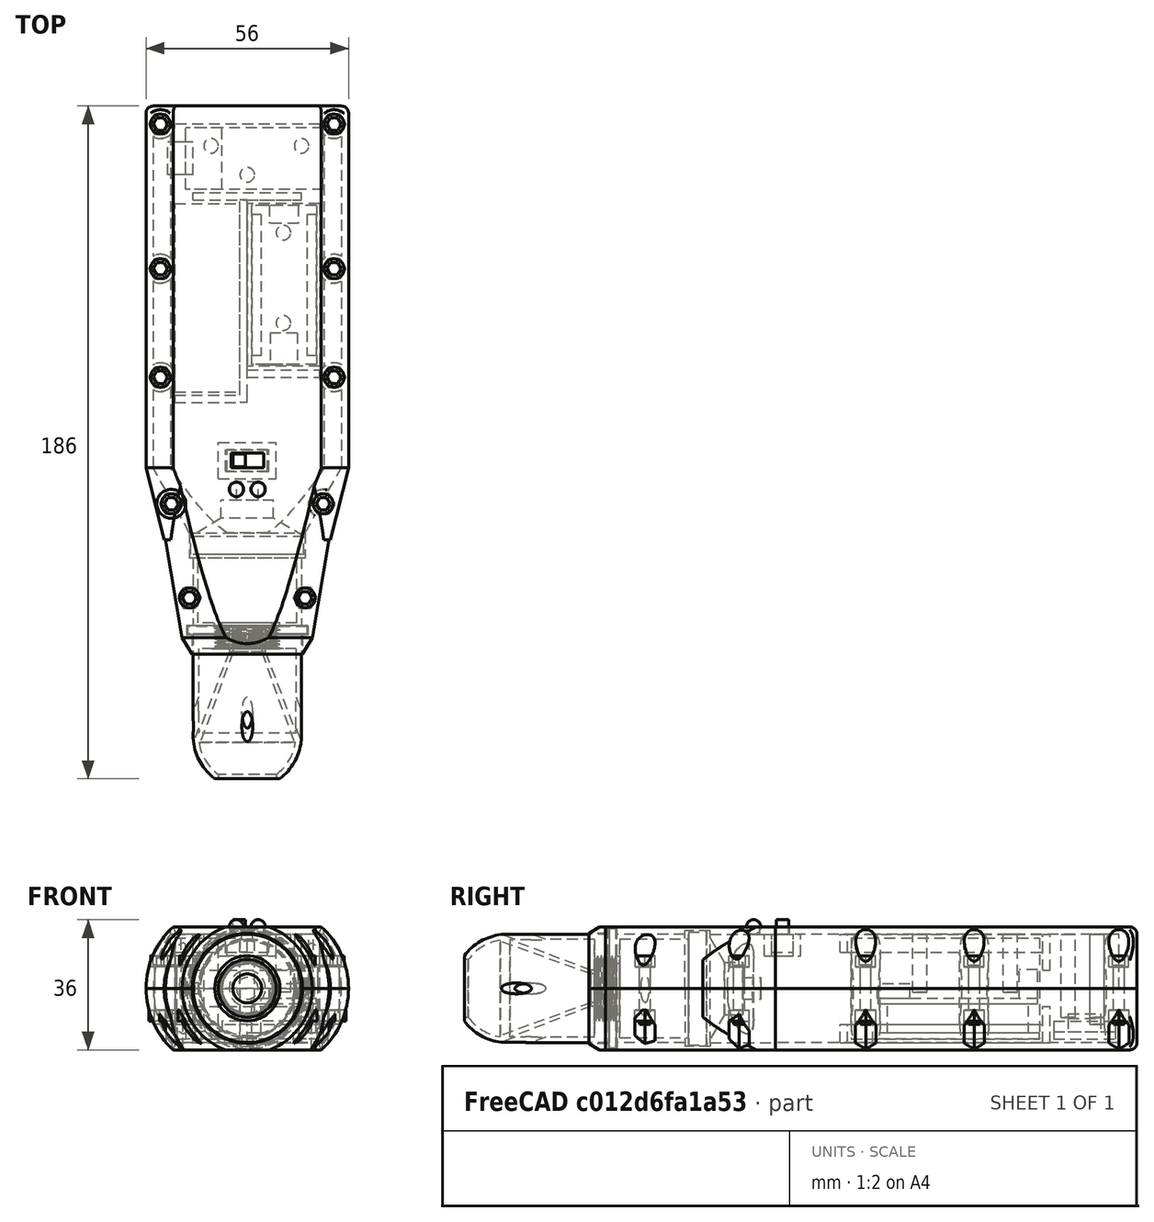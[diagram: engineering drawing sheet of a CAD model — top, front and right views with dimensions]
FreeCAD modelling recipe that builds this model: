
FCSTD DOCUMENT  (FreeCAD 0.15R4671 (Git))
Label: NitroxAnalyzer
License: All rights reserved
LicenseURL: http://en.wikipedia.org/wiki/All_rights_reserved
objects: Part::Cylinder×71, Part::MultiFuse×69, Part::Feature×42, Part::Box×36, Part::Cut×30, Part::Cone×12, Raytracing::RayFeature×11, Part::Sphere×4, Part::Fillet×2, Part::MultiCommon×2, Part::RegularPolygon×2, Part::Extrusion×2, Raytracing::RayProject×1
note: 272 computed .brp shape members not serialized (recipe doc carries the construction recipe); baked Part::Feature solids carry a one-line shape summary decoded from their .brp

FEATURE [Part::Cylinder] Cylinder
  Angle = 360
  Height = 2
  Placement = pos=(0,46,0) rot=(1,0,0;1.5708rad)
  Radius = 16.5
FEATURE [Part::Cylinder] Cylinder001
  Angle = 360
  Height = 28
  Placement = pos=(0,44,0) rot=(1,0,0;1.5708rad)
  Radius = 15
FEATURE [Part::Sphere] Sphere
  Angle1 = -90
  Angle2 = 90
  Angle3 = 180
  Placement = pos=(0,16,0) rot=(0,0,1;3.14159rad)
  Radius = 15
FEATURE [Part::Sphere] Sphere001
  Angle1 = -90
  Angle2 = 90
  Angle3 = 180
  Placement = pos=(0,16,0) rot=(0,0,1;3.14159rad)
  Radius = 13.5
FEATURE [Part::Cut] Cut
  Base = -> Sphere
  Tool = -> Sphere001
FEATURE [Part::Box] Box  label="Cube"
  Height = 30
  Length = 30
  Placement = pos=(-15,-6,-15) rot=(0,0,1;0rad)
  Width = 10
FEATURE [Part::Cut] Cut001
  Base = -> Cut
  Tool = -> Box
FEATURE [Part::Cylinder] Cylinder002
  Angle = 360
  Height = 24
  Placement = pos=(0,40,0) rot=(1,0,0;1.5708rad)
  Radius = 13.5
FEATURE [Part::Cut] Cut002
  Base = -> Cylinder001
  Tool = -> Cylinder002
FEATURE [Part::MultiFuse] Fusion
  Shapes = -> [Cut002,Cut001]
FEATURE [Part::Feature] Cut003
  Placement = pos=(-50,16,-24) rot=(0,0,1;0rad)
  shape: bbox 28.06 x 6.962 x 28.06 mm, 14 faces (baked)
FEATURE [Part::Cylinder] Cylinder003
  Angle = 360
  Height = 6
  Placement = pos=(0,46,0) rot=(1,0,0;1.5708rad)
  Radius = 10
FEATURE [Part::MultiFuse] Fusion001
  Shapes = -> [Cylinder,Fusion]
FEATURE [Part::Cut] Cut004
  Base = -> Fusion001
  Tool = -> Cylinder003
FEATURE [Part::MultiFuse] Fusion002
  Shapes = -> [Cut004,Cut003]
FEATURE [Part::Cone] Cone
  Angle = 360
  Height = 25
  Placement = pos=(0,46,0) rot=(1,0,0;1.5708rad)
  Radius1 = 5
  Radius2 = 14.5
FEATURE [Part::Cone] Cone001
  Angle = 360
  Height = 25
  Placement = pos=(0,46,0) rot=(1,0,0;1.5708rad)
  Radius1 = 4
  Radius2 = 13
FEATURE [Part::Cut] Cut005
  Base = -> Cone
  Placement = pos=(0,-7,0) rot=(0,0,1;0rad)
  Tool = -> Cone001
FEATURE [Part::Cylinder] Cylinder004
  Angle = 360
  Height = 7
  Placement = pos=(0,46,0) rot=(1,0,0;1.5708rad)
  Radius = 5
FEATURE [Part::Cylinder] Cylinder005
  Angle = 360
  Height = 7
  Placement = pos=(0,46,0) rot=(1,0,0;1.5708rad)
  Radius = 4
FEATURE [Part::Cut] Cut006
  Base = -> Cylinder004
  Tool = -> Cylinder005
FEATURE [Part::MultiFuse] Fusion003
  Shapes = -> [Cut005,Cut006]
FEATURE [Part::MultiFuse] Fusion004
  Shapes = -> [Fusion002,Fusion003]
FEATURE [Part::Cylinder] Cylinder006
  Angle = 360
  Height = 50
  Placement = pos=(0,37,8) rot=(1,0,0;1.213rad)
  Radius = 1.5
FEATURE [Part::Feature] Cylinder007
  Placement = pos=(0,0,0) rot=(0,1,0;1.5708rad)
  shape: bbox 20.32 x 47.88 x 3 mm, 3 faces (baked)
FEATURE [Part::Feature] Cylinder008
  Placement = pos=(0,0,0) rot=(0,1,0;3.14159rad)
  shape: bbox 3 x 47.88 x 20.32 mm, 3 faces (baked)
FEATURE [Part::Feature] Cylinder009
  Placement = pos=(0,0,0) rot=(0,-1,0;1.5708rad)
  shape: bbox 20.32 x 47.88 x 3 mm, 3 faces (baked)
FEATURE [Part::MultiFuse] Fusion005
  Shapes = -> [Cylinder009,Cylinder008,Cylinder007,Cylinder006]
FEATURE [Part::Cut] Cut007
  Base = -> Fusion004
  Tool = -> Fusion005
FEATURE [Part::Cylinder] Cylinder010
  Angle = 360
  Height = 18
  Placement = pos=(0,10,0) rot=(1,0,0;1.5708rad)
  Radius = 8
FEATURE [Part::Cut] Cut008  label="o2-cell-support"
  Base = -> Cut007
  Tool = -> Cylinder010
FEATURE [Part::Feature] Fusion006  label="o2_cell"
  Placement = pos=(-62,-6,-24) rot=(0,0,1;0rad)
  shape: bbox 31.3 x 45 x 31.3 mm, 15 faces (baked)
FEATURE [Part::Box] Box004  label="battery"
  Height = 18
  Length = 28
  Placement = pos=(-20,111,14) rot=(0,1,0;1.5708rad)
  Width = 52
FEATURE [Part::Cylinder] Cylinder032
  Angle = 360
  Height = 100
  Placement = pos=(5,190,0) rot=(1,0,0;1.5708rad)
  Radius = 23
FEATURE [Part::Cylinder] Cylinder033
  Angle = 360
  Height = 100
  Placement = pos=(-5,190,0) rot=(1,0,0;1.5708rad)
  Radius = 23
FEATURE [Part::MultiFuse] Fusion017
  Shapes = -> [Cylinder033,Cylinder032]
FEATURE [Part::Box] Box012  label="Cube010"
  Height = 18
  Length = 47
  Placement = pos=(-24,0,17) rot=(0,0,1;0rad)
  Width = 200
FEATURE [Part::Box] Box013  label="Cube011"
  Height = 18
  Length = 47
  Placement = pos=(-24,0,-35) rot=(0,0,1;0rad)
  Width = 200
FEATURE [Part::MultiFuse] Fusion018
  Shapes = -> [Box013,Box012]
FEATURE [Part::Cone] Cone006
  Angle = 360
  Height = 20
  Placement = pos=(5,70,0) rot=(-1,0,0;1.5708rad)
  Radius1 = 18
  Radius2 = 23
FEATURE [Part::Cone] Cone007
  Angle = 360
  Height = 20
  Placement = pos=(-5,70,0) rot=(-1,0,0;1.5708rad)
  Radius1 = 18
  Radius2 = 23
FEATURE [Part::Cone] Cone008
  Angle = 360
  Height = 47
  Placement = pos=(0,43,0) rot=(-1,0,0;1.5708rad)
  Radius1 = 18
  Radius2 = 26
FEATURE [Part::MultiFuse] Fusion019
  Shapes = -> [Cone008,Cone007,Cone006]
FEATURE [Part::MultiFuse] Fusion020
  Shapes = -> [Fusion017,Fusion019]
FEATURE [Part::Cut] Cut026
  Base = -> Fusion020
  Tool = -> Fusion018
FEATURE [Part::Cylinder] Cylinder038
  Angle = 360
  Height = 6
  Placement = pos=(0,44,0) rot=(1,0,0;1.5708rad)
  Radius = 15.25
FEATURE [Part::Cone] Cone016
  Angle = 360
  Height = 5
  Placement = pos=(0,38,0) rot=(-1,0,0;1.5708rad)
  Radius1 = 15
  Radius2 = 18
FEATURE [Part::Box] Box016  label="Cube014"
  Height = 18
  Length = 47
  Placement = pos=(-24,0,15) rot=(0,0,1;0rad)
  Width = 200
FEATURE [Part::Box] Box017  label="Cube015"
  Height = 18
  Length = 47
  Placement = pos=(-24,0,-33) rot=(0,0,1;0rad)
  Width = 200
FEATURE [Part::MultiFuse] Fusion029
  Shapes = -> [Box017,Box016]
FEATURE [Part::Cylinder] Cylinder039
  Angle = 360
  Height = 20
  Placement = pos=(0,65,0) rot=(1,0,0;1.5708rad)
  Radius = 15
FEATURE [Part::Cylinder] Cylinder040
  Angle = 360
  Height = 2.5
  Placement = pos=(0,46.25,0) rot=(1,0,0;1.5708rad)
  Radius = 16.75
FEATURE [Part::Cylinder] Cylinder041
  Angle = 360
  Height = 7
  Placement = pos=(0,72,0) rot=(1,0,0;1.5708rad)
  Radius = 16
FEATURE [Part::Cone] Cone017
  Angle = 360
  Height = 18
  Placement = pos=(0,72,0) rot=(-1,0,0;1.5708rad)
  Radius1 = 16
  Radius2 = 26
FEATURE [Part::Box] Box018  label="Cube016"
  Height = 15
  Length = 47
  Placement = pos=(-24,0,15) rot=(0,0,1;0rad)
  Width = 200
FEATURE [Part::Box] Box019  label="Cube017"
  Height = 15
  Length = 47
  Placement = pos=(-24,0,-30) rot=(0,0,1;0rad)
  Width = 200
FEATURE [Part::MultiFuse] Fusion030
  Shapes = -> [Box019,Box018]
FEATURE [Part::Cylinder] Cylinder042
  Angle = 360
  Height = 95
  Placement = pos=(0,185,0) rot=(1,0,0;1.5708rad)
  Radius = 26
FEATURE [Part::MultiFuse] Fusion031
  Shapes = -> [Cone017,Cylinder042]
FEATURE [Part::Cut] Cut031
  Base = -> Fusion031
  Tool = -> Fusion030
FEATURE [Part::MultiFuse] Fusion032
  Shapes = -> [Cylinder039,Cylinder040,Cylinder041,Cut031]
FEATURE [Part::Box] Box020  label="Cube018"
  Height = 1.6
  Length = 20
  Width = 45
FEATURE [Part::Box] Box021  label="Cube019"
  Height = 8
  Length = 2.54
  Width = 39
FEATURE [Part::Box] Box022  label="Cube020"
  Height = 8
  Length = 2.54
  Placement = pos=(15.24,0,0) rot=(0,0,1;0rad)
  Width = 39
FEATURE [Part::MultiFuse] Fusion036
  Placement = pos=(1,3,1.6) rot=(0,0,1;0rad)
  Shapes = -> [Box022,Box021]
FEATURE [Part::Box] Box023  label="Cube021"
  Height = 1.6
  Length = 18
  Placement = pos=(0.9,0.5,9.6) rot=(0,0,1;0rad)
  Width = 44
FEATURE [Part::Box] Box024  label="Cube022"
  Height = 8
  Length = 8
  Placement = pos=(5.9,0.5,11.2) rot=(0,0,1;0rad)
  Width = 5
FEATURE [Part::Box] Box025  label="Cube023"
  Height = 4
  Length = 7.5
  Placement = pos=(6.175,35.75,11.2) rot=(0,0,1;0rad)
  Width = 9
FEATURE [Part::MultiFuse] Fusion037  label="arduino nano"
  Shapes = -> [Box024,Box023,Box025]
FEATURE [Part::MultiFuse] Fusion038  label="nano support"
  Shapes = -> [Fusion036,Box020]
FEATURE [Part::MultiFuse] Fusion039  label="nano board"
  Placement = pos=(20,163,-14) rot=(0,0,1;3.14159rad)
  Shapes = -> [Fusion038,Fusion037]
FEATURE [Part::Feature] Fusion042  label="BT006"
  Placement = pos=(111,164,-43) rot=(0,0,1;1.5708rad)
  shape: bbox 43 x 17 x 7 mm, 14 faces (baked)
FEATURE [Part::MultiFuse] Fusion043
  Shapes = -> [Cut026,Cone016]
FEATURE [Part::Cut] Cut032
  Base = -> Fusion043
  Tool = -> Cylinder038
FEATURE [Part::Cut] Cut033
  Base = -> Cut032
  Tool = -> Fusion029
FEATURE [Part::Cut] Cut034
  Base = -> Cut033
  Tool = -> Fusion032
FEATURE [Part::Fillet] Fillet  label="BOX"
  Base = -> Cut034
  Edges = 5 edges r=2: [Edge15,Edge25,Edge38,Edge39,Edge40]
FEATURE [Part::Box] Box026  label="Cube024"
  Height = 10
  Length = 30
  Placement = pos=(-15,164,-15) rot=(0,0,1;0rad)
  Width = 2
FEATURE [Part::Cylinder] Cylinder043
  Angle = 360
  Height = 23
  Placement = pos=(15,179,-8) rot=(0,0,1;0rad)
  Radius = 2
FEATURE [Part::Cylinder] Cylinder044
  Angle = 360
  Height = 23
  Placement = pos=(0,171,-8) rot=(0,0,1;0rad)
  Radius = 2
FEATURE [Part::Cylinder] Cylinder045
  Angle = 360
  Height = 25
  Placement = pos=(-10,179,-10) rot=(0,0,1;0rad)
  Radius = 2
FEATURE [Part::Box] Box028  label="Cube026"
  Height = 5
  Length = 56
  Placement = pos=(0,108,-15) rot=(0,0,1;1.5708rad)
  Width = 2
FEATURE [Part::Box] Box029  label="Cube027"
  Height = 5
  Length = 20
  Placement = pos=(-20,108,-15) rot=(0,0,1;0rad)
  Width = 2
FEATURE [Part::Cylinder] Cylinder046
  Angle = 360
  Height = 16
  Placement = pos=(10,144,-1) rot=(0,0,1;0rad)
  Radius = 2
FEATURE [Part::Box] Box030  label="Cube028"
  Height = 5
  Length = 20
  Placement = pos=(0,115,-15) rot=(0,0,1;0rad)
  Width = 2
FEATURE [Part::Box] Box031  label="Cube029"
  Height = 4
  Length = 3.5
  Placement = pos=(2,1.25,5) rot=(0,0,1;0rad)
  Width = 3.5
FEATURE [Part::Box] Box032  label="Cube030"
  Height = 5
  Length = 12
  Width = 6
FEATURE [Part::MultiFuse] Fusion044  label="power-switch"
  Placement = pos=(-6,89,10) rot=(0,0,1;0rad)
  Shapes = -> [Box032,Box031]
FEATURE [Part::Box] Box033  label="Cube031"
  Height = 4
  Length = 9
  Placement = pos=(-4.5,90,14) rot=(0,0,1;0rad)
  Width = 4
FEATURE [Part::Cut] Cut035  label="BOTTOM_BOX"
  Base = -> Fillet
  Tool = -> Box033
FEATURE [Part::Cylinder] Cylinder047
  Angle = 360
  Height = 40
  Placement = pos=(-16,54,-20) rot=(0,0,1;0rad)
  Radius = 1.5
FEATURE [Part::Cylinder] Cylinder048
  Angle = 360
  Height = 40
  Placement = pos=(16,54,-20) rot=(0,0,1;0rad)
  Radius = 1.5
FEATURE [Part::Cylinder] Cylinder049
  Angle = 360
  Height = 40
  Placement = pos=(-21,80,-20) rot=(0,0,1;0rad)
  Radius = 1.5
FEATURE [Part::Cylinder] Cylinder050
  Angle = 360
  Height = 40
  Placement = pos=(24,115,-20) rot=(0,0,1;0rad)
  Radius = 1.5
FEATURE [Part::Cylinder] Cylinder051
  Angle = 360
  Height = 40
  Placement = pos=(21,80,-20) rot=(0,0,1;0rad)
  Radius = 1.5
FEATURE [Part::Cylinder] Cylinder052
  Angle = 360
  Height = 40
  Placement = pos=(-24,115,-20) rot=(0,0,1;0rad)
  Radius = 1.5
FEATURE [Part::Cylinder] Cylinder053
  Angle = 360
  Height = 40
  Placement = pos=(24,115,-20) rot=(0,0,1;0rad)
  Radius = 1.5
FEATURE [Part::Cylinder] Cylinder054
  Angle = 360
  Height = 40
  Placement = pos=(-24,115,-20) rot=(0,0,1;0rad)
  Radius = 1.5
FEATURE [Part::MultiFuse] Fusion045
  Placement = pos=(0,30,0) rot=(0,0,1;0rad)
  Shapes = -> [Cylinder054,Cylinder053]
FEATURE [Part::Cylinder] Cylinder055
  Angle = 360
  Height = 40
  Placement = pos=(24,115,-20) rot=(0,0,1;0rad)
  Radius = 1.5
FEATURE [Part::Cylinder] Cylinder056
  Angle = 360
  Height = 40
  Placement = pos=(-24,115,-20) rot=(0,0,1;0rad)
  Radius = 1.5
FEATURE [Part::MultiFuse] Fusion046
  Placement = pos=(0,70,0) rot=(0,0,1;0rad)
  Shapes = -> [Cylinder056,Cylinder055]
FEATURE [Part::MultiFuse] Fusion047  label="holes"
  Shapes = -> [Fusion046,Fusion045,Cylinder052,Cylinder051,Cylinder050,Cylinder049,Cylinder048,Cylinder047]
FEATURE [Part::Cylinder] Cylinder057
  Angle = 360
  Height = 100
  Placement = pos=(5,190,0) rot=(1,0,0;1.5708rad)
  Radius = 23
FEATURE [Part::Cylinder] Cylinder058
  Angle = 360
  Height = 100
  Placement = pos=(-5,190,0) rot=(1,0,0;1.5708rad)
  Radius = 23
FEATURE [Part::MultiFuse] Fusion048
  Shapes = -> [Cylinder058,Cylinder057]
FEATURE [Part::Box] Box034  label="Cube032"
  Height = 18
  Length = 47
  Placement = pos=(-24,0,17) rot=(0,0,1;0rad)
  Width = 200
FEATURE [Part::Box] Box035  label="Cube033"
  Height = 18
  Length = 47
  Placement = pos=(-24,0,-35) rot=(0,0,1;0rad)
  Width = 200
FEATURE [Part::MultiFuse] Fusion049
  Shapes = -> [Box035,Box034]
FEATURE [Part::Cone] Cone018
  Angle = 360
  Height = 20
  Placement = pos=(5,70,0) rot=(-1,0,0;1.5708rad)
  Radius1 = 18
  Radius2 = 23
FEATURE [Part::Cone] Cone019
  Angle = 360
  Height = 20
  Placement = pos=(-5,70,0) rot=(-1,0,0;1.5708rad)
  Radius1 = 18
  Radius2 = 23
FEATURE [Part::Cone] Cone020
  Angle = 360
  Height = 47
  Placement = pos=(0,43,0) rot=(-1,0,0;1.5708rad)
  Radius1 = 18
  Radius2 = 26
FEATURE [Part::MultiFuse] Fusion050
  Shapes = -> [Cone020,Cone019,Cone018]
FEATURE [Part::MultiFuse] Fusion051
  Shapes = -> [Fusion048,Fusion050]
FEATURE [Part::Cut] Cut036
  Base = -> Fusion051
  Tool = -> Fusion049
FEATURE [Part::Cylinder] Cylinder059
  Angle = 360
  Height = 6
  Placement = pos=(0,44,0) rot=(1,0,0;1.5708rad)
  Radius = 15.25
FEATURE [Part::Cone] Cone021
  Angle = 360
  Height = 5
  Placement = pos=(0,38,0) rot=(-1,0,0;1.5708rad)
  Radius1 = 15
  Radius2 = 18
FEATURE [Part::Box] Box036  label="Cube034"
  Height = 18
  Length = 47
  Placement = pos=(-24,0,15) rot=(0,0,1;0rad)
  Width = 200
FEATURE [Part::Box] Box037  label="Cube035"
  Height = 18
  Length = 47
  Placement = pos=(-24,0,-33) rot=(0,0,1;0rad)
  Width = 200
FEATURE [Part::MultiFuse] Fusion052
  Shapes = -> [Box037,Box036]
FEATURE [Part::Cylinder] Cylinder060
  Angle = 360
  Height = 20
  Placement = pos=(0,65,0) rot=(1,0,0;1.5708rad)
  Radius = 15
FEATURE [Part::Cylinder] Cylinder061
  Angle = 360
  Height = 2.5
  Placement = pos=(0,46.25,0) rot=(1,0,0;1.5708rad)
  Radius = 16.75
FEATURE [Part::Cylinder] Cylinder062
  Angle = 360
  Height = 7
  Placement = pos=(0,72,0) rot=(1,0,0;1.5708rad)
  Radius = 16
FEATURE [Part::Cone] Cone022
  Angle = 360
  Height = 18
  Placement = pos=(0,72,0) rot=(-1,0,0;1.5708rad)
  Radius1 = 16
  Radius2 = 26
FEATURE [Part::Box] Box038  label="Cube036"
  Height = 15
  Length = 47
  Placement = pos=(-24,0,15) rot=(0,0,1;0rad)
  Width = 200
FEATURE [Part::Box] Box039  label="Cube037"
  Height = 15
  Length = 47
  Placement = pos=(-24,0,-30) rot=(0,0,1;0rad)
  Width = 200
FEATURE [Part::MultiFuse] Fusion053
  Shapes = -> [Box039,Box038]
FEATURE [Part::Cylinder] Cylinder063
  Angle = 360
  Height = 95
  Placement = pos=(0,185,0) rot=(1,0,0;1.5708rad)
  Radius = 26
FEATURE [Part::MultiFuse] Fusion054
  Shapes = -> [Cone022,Cylinder063]
FEATURE [Part::Cut] Cut037
  Base = -> Fusion054
  Tool = -> Fusion053
FEATURE [Part::MultiFuse] Fusion055
  Shapes = -> [Cylinder060,Cylinder061,Cylinder062,Cut037]
FEATURE [Part::MultiFuse] Fusion056
  Shapes = -> [Cut036,Cone021]
FEATURE [Part::Cut] Cut038
  Base = -> Fusion056
  Tool = -> Cylinder059
FEATURE [Part::Cut] Cut039
  Base = -> Cut038
  Tool = -> Fusion052
FEATURE [Part::Cut] Cut040
  Base = -> Cut039
  Tool = -> Fusion055
FEATURE [Part::Fillet] Fillet001  label="BOX001"
  Base = -> Cut040
  Edges = 5 edges r=2: [Edge15,Edge25,Edge38,Edge39,Edge40]
FEATURE [Part::Box] Box040  label="Cube038"
  Height = 4
  Length = 9
  Placement = pos=(-4.5,90,14) rot=(0,0,1;0rad)
  Width = 4
FEATURE [Part::Cut] Cut041  label="TOP_BOX"
  Base = -> Fillet001
  Tool = -> Box040
FEATURE [Part::Box] Box041  label="Cube039"
  Height = 30
  Length = 100
  Placement = pos=(-39,-4,0) rot=(0,0,1;0rad)
  Width = 300
FEATURE [Part::Cut] Cut042
  Base = -> Cut035
  Tool = -> Box041
FEATURE [Part::Cylinder] Cylinder064
  Angle = 360
  Height = 40
  Placement = pos=(-16,54,-20) rot=(0,0,1;0rad)
  Radius = 1.5
FEATURE [Part::Cylinder] Cylinder065
  Angle = 360
  Height = 40
  Placement = pos=(16,54,-20) rot=(0,0,1;0rad)
  Radius = 1.5
FEATURE [Part::Cylinder] Cylinder066
  Angle = 360
  Height = 40
  Placement = pos=(-21,80,-20) rot=(0,0,1;0rad)
  Radius = 4
FEATURE [Part::Cylinder] Cylinder067
  Angle = 360
  Height = 40
  Placement = pos=(24,115,-20) rot=(0,0,1;0rad)
  Radius = 4
FEATURE [Part::Cylinder] Cylinder068
  Angle = 360
  Height = 40
  Placement = pos=(21,80,-20) rot=(0,0,1;0rad)
  Radius = 4
FEATURE [Part::Cylinder] Cylinder069
  Angle = 360
  Height = 40
  Placement = pos=(-24,115,-20) rot=(0,0,1;0rad)
  Radius = 4
FEATURE [Part::Cylinder] Cylinder070
  Angle = 360
  Height = 40
  Placement = pos=(24,115,-20) rot=(0,0,1;0rad)
  Radius = 4
FEATURE [Part::Cylinder] Cylinder071
  Angle = 360
  Height = 40
  Placement = pos=(-24,115,-20) rot=(0,0,1;0rad)
  Radius = 4
FEATURE [Part::MultiFuse] Fusion057
  Placement = pos=(0,30,0) rot=(0,0,1;0rad)
  Shapes = -> [Cylinder071,Cylinder070]
FEATURE [Part::Cylinder] Cylinder072
  Angle = 360
  Height = 40
  Placement = pos=(24,115,-20) rot=(0,0,1;0rad)
  Radius = 4
FEATURE [Part::Cylinder] Cylinder073
  Angle = 360
  Height = 40
  Placement = pos=(-24,115,-20) rot=(0,0,1;0rad)
  Radius = 4
FEATURE [Part::MultiFuse] Fusion058
  Placement = pos=(0,70,0) rot=(0,0,1;0rad)
  Shapes = -> [Cylinder073,Cylinder072]
FEATURE [Part::MultiFuse] Fusion059
  Placement = pos=(0,0,-20) rot=(0,0,1;0rad)
  Shapes = -> [Fusion058,Fusion057,Cylinder069,Cylinder068,Cylinder067,Cylinder066,Cylinder065,Cylinder064]
FEATURE [Part::MultiFuse] Fusion060
  Shapes = -> [Box030,Box029,Box028,Box026]
FEATURE [Part::Box] Box042  label="Cube040"
  Height = 80
  Length = 60
  Placement = pos=(-30,0,-80) rot=(0,0,1;0rad)
  Width = 200
FEATURE [Part::Feature] Cut043
  shape: bbox 56 x 147 x 47.44 mm, 14 faces (baked)
FEATURE [Part::MultiCommon] Common
  Shapes = -> [Fusion059,Cut043]
FEATURE [Part::MultiFuse] Fusion061
  Shapes = -> [Cut042,Common]
FEATURE [Part::Cut] Cut044
  Base = -> Fusion061
  Tool = -> Fusion047
FEATURE [Part::Cylinder] Cylinder074
  Angle = 360
  Height = 16
  Placement = pos=(0,0,-9) rot=(0,0,1;0rad)
  Radius = 1.5
FEATURE [Part::Feature] Extrude001
  Placement = pos=(21,80,-36) rot=(0,0,1;0rad)
  shape: bbox 6.5 x 5.629 x 30 mm, 8 faces (baked)
FEATURE [Part::Cylinder] Cylinder075
  Angle = 360
  Height = 3
  Placement = pos=(0,0,7) rot=(0,0,1;0rad)
  Radius = 2.75
FEATURE [Part::MultiFuse] Fusion062
  Placement = pos=(16,54,-1) rot=(0,0,1;0rad)
  Shapes = -> [Cylinder075,Cylinder074]
FEATURE [Part::Feature] Extrude002
  Placement = pos=(-21,80,-36) rot=(0,0,1;0rad)
  shape: bbox 6.5 x 5.629 x 30 mm, 8 faces (baked)
FEATURE [Part::MultiFuse] Fusion063
  Shapes = -> [Extrude002,Extrude001]
FEATURE [Part::Feature] Extrude003
  Placement = pos=(24,80,-36) rot=(0,0,1;0rad)
  shape: bbox 6.5 x 5.629 x 30 mm, 8 faces (baked)
FEATURE [Part::Feature] Extrude004
  Placement = pos=(-24,80,-36) rot=(0,0,1;0rad)
  shape: bbox 6.5 x 5.629 x 30 mm, 8 faces (baked)
FEATURE [Part::MultiFuse] Fusion064
  Placement = pos=(0,35,0) rot=(0,0,1;0rad)
  Shapes = -> [Extrude004,Extrude003]
FEATURE [Part::Feature] Fusion065
  Placement = pos=(0,30,0) rot=(0,0,1;0rad)
  shape: bbox 54.5 x 5.629 x 30 mm, 16 faces, 2 solids (baked)
FEATURE [Part::Feature] Fusion066
  Placement = pos=(0,70,0) rot=(0,0,1;0rad)
  shape: bbox 54.5 x 5.629 x 30 mm, 16 faces, 2 solids (baked)
FEATURE [Part::MultiFuse] Fusion067
  Shapes = -> [Fusion066,Fusion065,Fusion064,Fusion063]
FEATURE [Part::Feature] Extrude005
  Placement = pos=(16,54,-36) rot=(0,0,1;0rad)
  shape: bbox 6.5 x 5.629 x 30 mm, 8 faces (baked)
FEATURE [Part::Cut] Cut045
  Base = -> Cut044
  Tool = -> Fusion067
FEATURE [Part::Feature] Extrude006
  Placement = pos=(-16,54,-36) rot=(0,0,1;0rad)
  shape: bbox 6.5 x 5.629 x 30 mm, 8 faces (baked)
FEATURE [Part::MultiFuse] Fusion068
  Shapes = -> [Extrude006,Extrude005]
FEATURE [Part::Cut] Cut046  label="box bottomdaf"
  Base = -> Cut045
  Tool = -> Fusion068
FEATURE [Part::MultiFuse] Fusion069  label="box-bottom"
  Shapes = -> [Fusion060,Cut046]
FEATURE [Part::Cut] Cut047
  Base = -> Cut041
  Tool = -> Box042
FEATURE [Part::Cylinder] Cylinder076
  Angle = 360
  Height = 40
  Placement = pos=(-16,54,-20) rot=(0,0,1;0rad)
  Radius = 1.5
FEATURE [Part::Cylinder] Cylinder077
  Angle = 360
  Height = 40
  Placement = pos=(16,54,-20) rot=(0,0,1;0rad)
  Radius = 1.5
FEATURE [Part::Cylinder] Cylinder078
  Angle = 360
  Height = 40
  Placement = pos=(-21,80,-20) rot=(0,0,1;0rad)
  Radius = 1.5
FEATURE [Part::Cylinder] Cylinder079
  Angle = 360
  Height = 40
  Placement = pos=(24,115,-20) rot=(0,0,1;0rad)
  Radius = 1.5
FEATURE [Part::Cylinder] Cylinder080
  Angle = 360
  Height = 40
  Placement = pos=(21,80,-20) rot=(0,0,1;0rad)
  Radius = 1.5
FEATURE [Part::Cylinder] Cylinder081
  Angle = 360
  Height = 40
  Placement = pos=(-24,115,-20) rot=(0,0,1;0rad)
  Radius = 1.5
FEATURE [Part::Cylinder] Cylinder082
  Angle = 360
  Height = 40
  Placement = pos=(24,115,-20) rot=(0,0,1;0rad)
  Radius = 1.5
FEATURE [Part::Cylinder] Cylinder083
  Angle = 360
  Height = 40
  Placement = pos=(-24,115,-20) rot=(0,0,1;0rad)
  Radius = 1.5
FEATURE [Part::MultiFuse] Fusion070
  Placement = pos=(0,30,0) rot=(0,0,1;0rad)
  Shapes = -> [Cylinder083,Cylinder082]
FEATURE [Part::Cylinder] Cylinder084
  Angle = 360
  Height = 40
  Placement = pos=(24,115,-20) rot=(0,0,1;0rad)
  Radius = 1.5
FEATURE [Part::Cylinder] Cylinder085
  Angle = 360
  Height = 40
  Placement = pos=(-24,115,-20) rot=(0,0,1;0rad)
  Radius = 1.5
FEATURE [Part::MultiFuse] Fusion071
  Placement = pos=(0,70,0) rot=(0,0,1;0rad)
  Shapes = -> [Cylinder085,Cylinder084]
FEATURE [Part::MultiFuse] Fusion072  label="holes001"
  Shapes = -> [Fusion071,Fusion070,Cylinder081,Cylinder080,Cylinder079,Cylinder078,Cylinder077,Cylinder076]
FEATURE [Part::Cylinder] Cylinder086
  Angle = 360
  Height = 40
  Placement = pos=(-16,54,-20) rot=(0,0,1;0rad)
  Radius = 1.5
FEATURE [Part::Cylinder] Cylinder087
  Angle = 360
  Height = 40
  Placement = pos=(16,54,-20) rot=(0,0,1;0rad)
  Radius = 1.5
FEATURE [Part::Cylinder] Cylinder088
  Angle = 360
  Height = 40
  Placement = pos=(-21,80,-20) rot=(0,0,1;0rad)
  Radius = 4
FEATURE [Part::Cylinder] Cylinder089
  Angle = 360
  Height = 40
  Placement = pos=(24,115,-20) rot=(0,0,1;0rad)
  Radius = 4
FEATURE [Part::Cylinder] Cylinder090
  Angle = 360
  Height = 40
  Placement = pos=(21,80,-20) rot=(0,0,1;0rad)
  Radius = 4
FEATURE [Part::Cylinder] Cylinder091
  Angle = 360
  Height = 40
  Placement = pos=(-24,115,-20) rot=(0,0,1;0rad)
  Radius = 4
FEATURE [Part::Cylinder] Cylinder092
  Angle = 360
  Height = 40
  Placement = pos=(24,115,-20) rot=(0,0,1;0rad)
  Radius = 4
FEATURE [Part::Cylinder] Cylinder093
  Angle = 360
  Height = 40
  Placement = pos=(-24,115,-20) rot=(0,0,1;0rad)
  Radius = 4
FEATURE [Part::MultiFuse] Fusion073
  Placement = pos=(0,30,0) rot=(0,0,1;0rad)
  Shapes = -> [Cylinder093,Cylinder092]
FEATURE [Part::Cylinder] Cylinder094
  Angle = 360
  Height = 40
  Placement = pos=(24,115,-20) rot=(0,0,1;0rad)
  Radius = 4
FEATURE [Part::Cylinder] Cylinder095
  Angle = 360
  Height = 40
  Placement = pos=(-24,115,-20) rot=(0,0,1;0rad)
  Radius = 4
FEATURE [Part::MultiFuse] Fusion074
  Placement = pos=(0,70,0) rot=(0,0,1;0rad)
  Shapes = -> [Cylinder095,Cylinder094]
FEATURE [Part::MultiFuse] Fusion075
  Placement = pos=(0,0,20) rot=(0,0,1;0rad)
  Shapes = -> [Fusion074,Fusion073,Cylinder091,Cylinder090,Cylinder089,Cylinder088,Cylinder087,Cylinder086]
FEATURE [Part::Feature] Cut048
  shape: bbox 56 x 147 x 47.44 mm, 14 faces (baked)
FEATURE [Part::MultiCommon] Common001
  Shapes = -> [Fusion075,Cut048]
FEATURE [Part::MultiFuse] Fusion076
  Shapes = -> [Cut047,Common001]
FEATURE [Part::Cut] Cut049
  Base = -> Fusion076
  Tool = -> Fusion072
FEATURE [Part::Feature] Fusion078
  Placement = pos=(16,54,0) rot=(0,0,1;0rad)
  shape: bbox 5.5 x 5.5 x 31 mm, 5 faces (baked)
FEATURE [Part::Feature] Fusion079
  Placement = pos=(-16,54,0) rot=(0,0,1;0rad)
  shape: bbox 5.5 x 5.5 x 31 mm, 5 faces (baked)
FEATURE [Part::Feature] Fusion080
  Placement = pos=(-21,80,0) rot=(0,0,1;0rad)
  shape: bbox 5.5 x 5.5 x 31 mm, 5 faces (baked)
FEATURE [Part::Feature] Fusion081
  Placement = pos=(21,80,0) rot=(0,0,1;0rad)
  shape: bbox 5.5 x 5.5 x 31 mm, 5 faces (baked)
FEATURE [Part::Feature] Fusion082
  Placement = pos=(24,115,0) rot=(0,0,1;0rad)
  shape: bbox 5.5 x 5.5 x 31 mm, 5 faces (baked)
FEATURE [Part::Feature] Fusion083
  Placement = pos=(-24,115,0) rot=(0,0,1;0rad)
  shape: bbox 5.5 x 5.5 x 31 mm, 5 faces (baked)
FEATURE [Part::MultiFuse] Fusion084
  Shapes = -> [Fusion082,Fusion083]
FEATURE [Part::Feature] Fusion085
  Placement = pos=(24,115,0) rot=(0,0,1;0rad)
  shape: bbox 5.5 x 5.5 x 31 mm, 5 faces (baked)
FEATURE [Part::Feature] Fusion086
  Placement = pos=(-24,115,0) rot=(0,0,1;0rad)
  shape: bbox 5.5 x 5.5 x 31 mm, 5 faces (baked)
FEATURE [Part::MultiFuse] Fusion087
  Placement = pos=(0,30,0) rot=(0,0,1;0rad)
  Shapes = -> [Fusion085,Fusion086]
FEATURE [Part::Feature] Fusion088
  Placement = pos=(24,115,0) rot=(0,0,1;0rad)
  shape: bbox 5.5 x 5.5 x 31 mm, 5 faces (baked)
FEATURE [Part::Feature] Fusion089
  Placement = pos=(-24,115,0) rot=(0,0,1;0rad)
  shape: bbox 5.5 x 5.5 x 31 mm, 5 faces (baked)
FEATURE [Part::MultiFuse] Fusion090
  Placement = pos=(0,70,0) rot=(0,0,1;0rad)
  Shapes = -> [Fusion088,Fusion089]
FEATURE [Part::MultiFuse] Fusion091
  Shapes = -> [Fusion090,Fusion087,Fusion084,Fusion081,Fusion079,Fusion078,Fusion080]
FEATURE [Part::Cut] Cut050
  Base = -> Cut049
  Tool = -> Fusion091
FEATURE [Part::Box] Box043  label="Cube041"
  Height = 10
  Length = 30
  Placement = pos=(-15,164,-20) rot=(0,0,1;0rad)
  Width = 2
FEATURE [Part::Box] Box044  label="Cube042"
  Height = 5
  Length = 56
  Placement = pos=(0,108,-15) rot=(0,0,1;1.5708rad)
  Width = 2
FEATURE [Part::Box] Box045  label="Cube043"
  Height = 5
  Length = 20
  Placement = pos=(-20,108,-15) rot=(0,0,1;0rad)
  Width = 2
FEATURE [Part::MultiFuse] Fusion092  label="Fusion09"
  Placement = pos=(0,0,25) rot=(0,0,1;0rad)
  Shapes = -> [Box045,Box044,Box043]
FEATURE [Part::Box] Box046  label="Cube044"
  Height = 6
  Length = 16
  Placement = pos=(-8,87,9) rot=(0,0,1;0rad)
  Width = 10
FEATURE [Part::Box] Box047  label="Cube045"
  Height = 4
  Length = 3.5
  Placement = pos=(2,1.25,5) rot=(0,0,1;0rad)
  Width = 3.5
FEATURE [Part::Box] Box048  label="Cube046"
  Height = 7
  Length = 11.25
  Width = 6
FEATURE [Part::MultiFuse] Fusion093  label="switch_on_off001"
  Placement = pos=(-5.625,89,8) rot=(0,0,1;0rad)
  Shapes = -> [Box048,Box047]
FEATURE [Part::Cut] Cut051
  Base = -> Box046
  Tool = -> Fusion093
FEATURE [Part::Cylinder] Cylinder098
  Angle = 360
  Height = 30
  Placement = pos=(-3,84,0) rot=(0,0,1;0rad)
  Radius = 1.75
FEATURE [Part::Cylinder] Cylinder099
  Angle = 360
  Height = 30
  Placement = pos=(3,84,0) rot=(0,0,1;0rad)
  Radius = 1.75
FEATURE [Part::MultiFuse] Fusion094
  Shapes = -> [Cylinder098,Cylinder099]
FEATURE [Part::Cut] Cut052
  Base = -> Cut050
  Tool = -> Fusion094
FEATURE [Part::MultiFuse] Fusion095
  Shapes = -> [Cut051,Cut052]
FEATURE [Part::MultiFuse] Fusion096
  Shapes = -> [Fusion092,Fusion095]
FEATURE [Part::Cylinder] Cylinder100
  Angle = 360
  Height = 16
  Placement = pos=(10,119,-1) rot=(0,0,1;0rad)
  Radius = 2
FEATURE [Part::MultiFuse] Fusion097
  Placement = pos=(0,11,0) rot=(0,0,1;0rad)
  Shapes = -> [Cylinder100,Cylinder046]
FEATURE [Part::MultiFuse] Fusion098
  Shapes = -> [Fusion097,Cylinder045,Cylinder044,Cylinder043]
FEATURE [Part::MultiFuse] Fusion099  label="box-top"
  Shapes = -> [Fusion096,Fusion098]
FEATURE [Part::RegularPolygon] RegularPolygon001  label="Regular polygon001"
  Circumradius = 3.25
  Polygon = 6
FEATURE [Part::Extrusion] Extrude007
  Base = -> RegularPolygon001
  Dir = (0,0,3)
  Placement = pos=(16,54,-9) rot=(0,0,1;0rad)
  Solid = true
FEATURE [Part::MultiFuse] Fusion100
  Shapes = -> [Fusion062,Extrude007]
FEATURE [Part::Feature] Fusion101
  Placement = pos=(-32,0,0) rot=(0,0,1;0rad)
  shape: bbox 6.5 x 5.629 x 19 mm, 14 faces (baked)
FEATURE [Part::Feature] Fusion102
  Placement = pos=(5,26,0) rot=(0,0,1;0rad)
  shape: bbox 6.5 x 5.629 x 19 mm, 14 faces (baked)
FEATURE [Part::Feature] Fusion103
  Placement = pos=(-37,26,0) rot=(0,0,1;0rad)
  shape: bbox 6.5 x 5.629 x 19 mm, 14 faces (baked)
FEATURE [Part::Sphere] Sphere004  label="red-led-bt-activity"
  Angle1 = -90
  Angle2 = 90
  Angle3 = 360
  Placement = pos=(3,84,17) rot=(0,0,1;0rad)
  Radius = 2
FEATURE [Part::Sphere] Sphere005  label="green-led-power"
  Angle1 = -90
  Angle2 = 90
  Angle3 = 360
  Placement = pos=(-3,84,17) rot=(0,0,1;0rad)
  Radius = 2
FEATURE [Part::Feature] Fusion104
  Placement = pos=(8,61,0) rot=(0,0,1;0rad)
  shape: bbox 6.5 x 5.629 x 19 mm, 14 faces (baked)
FEATURE [Part::Feature] Fusion105
  Placement = pos=(-40,61,0) rot=(0,0,1;0rad)
  shape: bbox 6.5 x 5.629 x 19 mm, 14 faces (baked)
FEATURE [Part::Feature] Fusion106
  Placement = pos=(8,91,0) rot=(0,0,1;0rad)
  shape: bbox 6.5 x 5.629 x 19 mm, 14 faces (baked)
FEATURE [Part::Feature] Fusion107
  Placement = pos=(-40,91,0) rot=(0,0,1;0rad)
  shape: bbox 6.5 x 5.629 x 19 mm, 14 faces (baked)
FEATURE [Part::Feature] Fusion108
  Placement = pos=(8,131,0) rot=(0,0,1;0rad)
  shape: bbox 6.5 x 5.629 x 19 mm, 14 faces (baked)
FEATURE [Part::Feature] Fusion109
  Placement = pos=(-40,131,0) rot=(0,0,1;0rad)
  shape: bbox 6.5 x 5.629 x 19 mm, 14 faces (baked)
FEATURE [Part::MultiFuse] Fusion110  label="Boulons"
  Shapes = -> [Fusion109,Fusion106,Fusion107,Fusion108,Fusion104,Fusion105,Fusion103,Fusion102,Fusion101,Fusion100]
FEATURE [Raytracing::RayFeature] Fusion110_View
  Result = <blob: 254217 chars omitted>
  Source = -> Fusion110
  Transparency = 0
FEATURE [Raytracing::RayFeature] Fusion042_View
  Result = <blob: 9211 chars omitted>
  Source = -> Fusion042
  Transparency = 0
FEATURE [Raytracing::RayFeature] Fusion099_View
  Result = <blob: 411464 chars omitted>
  Source = -> Fusion099
  Transparency = 0
FEATURE [Raytracing::RayFeature] Fusion006_View
  Result = <blob: 135641 chars omitted>
  Source = -> Fusion006
  Transparency = 77
FEATURE [Raytracing::RayFeature] Cut008_View
  Result = <blob: 781493 chars omitted>
  Source = -> Cut008
  Transparency = 0
FEATURE [Raytracing::RayFeature] Sphere004_View
  Result = <blob: 21721 chars omitted>
  Source = -> Sphere004
  Transparency = 0
FEATURE [Raytracing::RayFeature] Sphere005_View
  Result = <blob: 21957 chars omitted>
  Source = -> Sphere005
  Transparency = 0
FEATURE [Raytracing::RayFeature] Box004_View
  Result = <blob: 2906 chars omitted>
  Source = -> Box004
  Transparency = 0
FEATURE [Raytracing::RayFeature] Fusion039_View
  Result = <blob: 15908 chars omitted>
  Source = -> Fusion039
  Transparency = 0
FEATURE [Raytracing::RayFeature] Fusion044_View
  Result = <blob: 4983 chars omitted>
  Source = -> Fusion044
  Transparency = 0
FEATURE [Raytracing::RayFeature] Fusion069_View
  Result = <blob: 324937 chars omitted>
  Source = -> Fusion069
  Transparency = 0
FEATURE [Raytracing::RayProject] PovProject
  Camera = // declares positon and view direction\n\n// Generated by FreeCAD (http://www.freecadweb.org/)\n#declare cam_location =  <69.6798,231.459,102.265>;\n#declare cam_look_at  = <3.81404,6.37167,96.7564>;\n#declare cam_sky      = <-0.512863,0.170667,-0.841335>;\n#declare cam_angle    = 45; \ncamera {\n  location  cam_location\n  look_at   cam_look_at\n  sky       cam_sky\n  angle     cam_angle \n  right x*3200/2400\n}
  Group = -> [Fusion110_View,Fusion042_View,Fusion099_View,Fusion006_View,Cut008_View,Sphere004_View,Sphere005_View,Box004_View,Fusion039_View,Fusion044_View,Fusion069_View]
  Template = C:/Program Files (x86)/FreeCAD 0.15/data/Mod/Raytracing/Templates/ProjectStd.pov
FEATURE [Part::RegularPolygon] RegularPolygon002  label="Regular polygon002"
  Circumradius = 2
  Polygon = 6
FEATURE [Part::Extrusion] Extrude009
  Base = -> RegularPolygon002
  Dir = (0,0,3)
  Placement = pos=(-16,54,6) rot=(0,0,1;0rad)
  Solid = true
FEATURE [Part::Feature] Extrude010
  Placement = pos=(16,54,6) rot=(0,0,1;0rad)
  shape: bbox 4 x 3.464 x 3 mm, 8 faces (baked)
FEATURE [Part::Feature] Extrude011
  Placement = pos=(-21,80,6) rot=(0,0,1;0rad)
  shape: bbox 4 x 3.464 x 3 mm, 8 faces (baked)
FEATURE [Part::Feature] Extrude012
  Placement = pos=(21,80,6) rot=(0,0,1;0rad)
  shape: bbox 4 x 3.464 x 3 mm, 8 faces (baked)
FEATURE [Part::Feature] Extrude013
  Placement = pos=(-24,115,6) rot=(0,0,1;0rad)
  shape: bbox 4 x 3.464 x 3 mm, 8 faces (baked)
FEATURE [Part::Feature] Extrude014
  Placement = pos=(24,115,6) rot=(0,0,1;0rad)
  shape: bbox 4 x 3.464 x 3 mm, 8 faces (baked)
FEATURE [Part::MultiFuse] Fusion111
  Shapes = -> [Extrude014,Extrude013]
FEATURE [Part::Feature] Fusion112
  Placement = pos=(0,70,0) rot=(0,0,1;0rad)
  shape: bbox 52 x 3.464 x 3 mm, 16 faces, 2 solids (baked)
FEATURE [Part::Feature] Fusion113
  Placement = pos=(0,30,0) rot=(0,0,1;0rad)
  shape: bbox 52 x 3.464 x 3 mm, 16 faces, 2 solids (baked)
FEATURE [Part::MultiFuse] Fusion114
  Placement = pos=(0,0,0.5) rot=(0,0,1;0rad)
  Shapes = -> [Fusion113,Fusion112,Fusion111,Extrude012,Extrude011,Extrude010,Extrude009]
FEATURE [Part::Cut] Cut053  label="nuts-and-bolts"
  Base = -> Fusion110
  Tool = -> Fusion114
FEATURE [Part::MultiFuse] Fusion115  label="sss"
  Shapes = -> [Fusion042,Fusion039,Box004,Fusion006]
FEATURE [Part::MultiFuse] Fusion116  label="ddd"
  Shapes = -> [Fusion115,Sphere005,Sphere004,Fusion044]
FEATURE [Part::MultiFuse] Fusion117  label="not-printable"
  Shapes = -> [Cut053,Fusion116]
